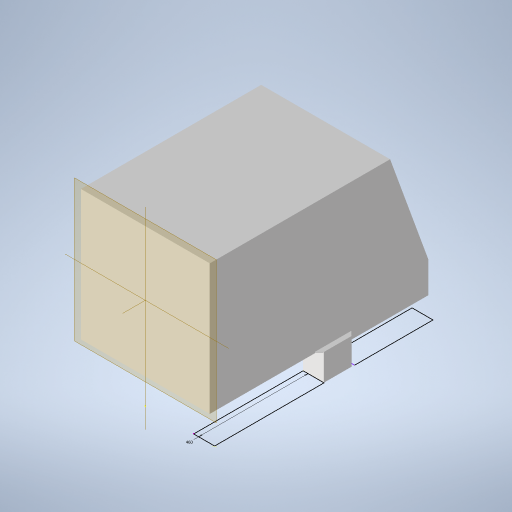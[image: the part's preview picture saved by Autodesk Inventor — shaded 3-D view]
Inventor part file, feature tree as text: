
AUTODESK INVENTOR PART (.ipt)
format: ipt  version: 2023 (Build 270158000, 158)  size: 317,440 bytes
history: native  units: mm
features: reference x18, other x16, extrude x8, sketch x7, plane x2
ambient origin geometry x8: Origin, YZ Plane, XZ Plane, XY Plane, X Axis, Y Axis, Z Axis, Center Point
bodies: Solid1 (feature_tree)
feature tree (51):
  plane  "Work Plane1"
  sketch  "Sketch1"  dims[d0=899.0mm d1=0.0mm d2=300.0mm]
  plane  "Work Plane2"
  extrude  "Extrusion1"  Depth=300.0mm
  extrude  "Extrusion2"  Depth=300.0mm
  sketch  "Sketch3"  dims[d6=10.0mm d7=0.0mm d8=460.0mm]
  extrude  "Extrusion3"  Depth=460.0mm
  extrude  "Extrusion4"  Depth=1.0mm
  extrude  "Extrusion5"  Depth=9.0mm TaperAngle=0.0deg
  extrude  "Extrusion6"  Depth=9.0mm TaperAngle=0.0deg
  extrude  "Extrusion7"  Depth=5.0mm TaperAngle=0.0deg
  extrude  "Extrusion8"  Depth=5.0mm
  reference  "Reference1"
  reference  "Reference2"
  reference  "Reference3"
  reference  "Reference4"
  reference  "Reference5"
  reference  "Reference6"
  reference  "Reference7"
  reference  "Reference8"
  reference  "Reference9"
  reference  "Reference10"
  reference  "Reference11"
  sketch  "Sketch2"  dims[d3=0.0mm d4=0.0mm d5=300.0mm]
  reference  "Reference12"
  sketch  "Sketch4"  dims[d9=10.0mm d10=0.0mm d11=1.0mm]
  reference  "Reference13"
  reference  "Reference14"
  sketch  "Sketch5"  dims[d12=1.0mm d13=9.0mm d14=0.0mm]
  reference  "Reference15"
  reference  "Reference16"
  sketch  "Sketch6"  dims[d15=1.0mm d16=9.0mm d17=0.0mm]
  reference  "Reference17"
  reference  "Reference18"
  sketch  "Sketch7"  dims[d18=5.0mm d19=10.0mm d20=0.0mm d21=100.0mm d22=160.0mm d23=0.0mm d24=0.0mm]
  parser-record x1  (decoder bookkeeping rows leaked as tree rows — omitted from the tree; the rows remain in map.json)
  other  "body.iam"
  other  "plate_front:1"
  other  "plate_top_03:1"
  other  "G_IC03_XX_12648V:1"
  other  "mount:1"
  other  "Roller track L 250:2"
  other  "PRO10282 Rollenleiste Abdeckung mit Seitenfuehrung 250:1"
  other  "Roller track L 178:2"
  other  "PRO10282 Rollenleiste Abdeckung mit Seitenfuehrung 178:1"
  other  "Cap 40_80:2"
  other  "Robotunits CAP_4080_1_ABS Plastic:1"
  other  "Roller track L 250:1"
  other  "Corner bracket 40_50:1"
  other  "GUS_4501_1:1"
  other  "Corner bracket 40_50:2"
note: 1 file-system path scrubbed to <path> (originals preserved in map.json)
